# Revit family: xxxBasin-Above_Counter-American_Standard-Boxe-050400X_Series
name_source: partatom
category: Plumbing Fixtures
units: mm (PartAtom-declared; Revit-internal decimal feet)

## family parameters
Always vertical = No
Cut with Voids When Loaded = No
OmniClass Number = 23.45.05.14.14
OmniClass Title = Sinks/Lavatories
Part Type = Normal
Room Calculation Point = No
Round Connector Dimension = Use Diameter
Shared = Yes
Work Plane-Based = Yes

## types (3) — shared parameters
ASME A112.19.2M for Vitreous China Fixtures = Yes
Assembly Code = D2010310
Basin Shape = Rectangle
Bowl Length = 11 1/4"
Bowl Width = 18 3/4"
CAN/CSA B45 series = Yes
CW Connection = Yes
CWFU = 1.5
Cold Water Connection Diameter = 1/2"
Cold Water Connection Height = 6 1/2"
Cold Water Connection Width = 4"
Compliance Certifications = A1995 National Building Code, section 3.7 and CAN/CSA - B651-M90 and OBC 3.7
Default Elevation = 31"
Finish = Vitreous China-American Standard-020-White
HW Connection = Yes
HWFU = 1.5
Height = 6 7/8"
Hot Water Connection Diameter = 1/2"
Hot Water Connection Height = 6 1/2"
Hot Water Connection Width = 4"
Installation Type = Above Counter
Length = 17 1/2"
Manufacturer = American Standard
Material = Vitreous China-American Standard-020-White
Overflow Location = Front
Price = Prices may vary. Please consult Manufacturer Representative for most up-to-date price list.
Product Documentation Link = https://americanstandard.box.com
Product Page URL = https://americanstandard.ca
Revised Date = 07/25/2022
URL = http://www.americanstandard.ca
Vent Connection = No
WFU = 2
Waste Connection = Yes
Waste Connection Diameter = 1 1/4"
Waste Connection Height = 8 3/4"
Width = 23 1/4"

## per-type parameters (varying)
| type | 0504 000 Less Faucet Holes | 0504 001 Centre Hole Only | 0504 008 Faucet Holes on 8" Centres | Centre Hole | Description | Faucet Constraint- 2 Centres | Faucet Hole- Centre Constraint |
| 0504.008.020 | No | No | Yes | Yes | Boxe Above Counter Sink with 8-Inch Widespread | 5" | 5" |
| 0504.000.020 | Yes | No | No | No | Boxe Above Counter Sink Less Holes | 2" | 2" |
| 0504.001.020 | No | Yes | No | Yes | Boxe Above Counter Sink with Centre Hole Only | 2" | 5" |

note: column(s) folded — value = type name in every type: Model

## geometry (parser evidence)
native form markers: Sweep x2
no freeform markers — native parametric forms only
